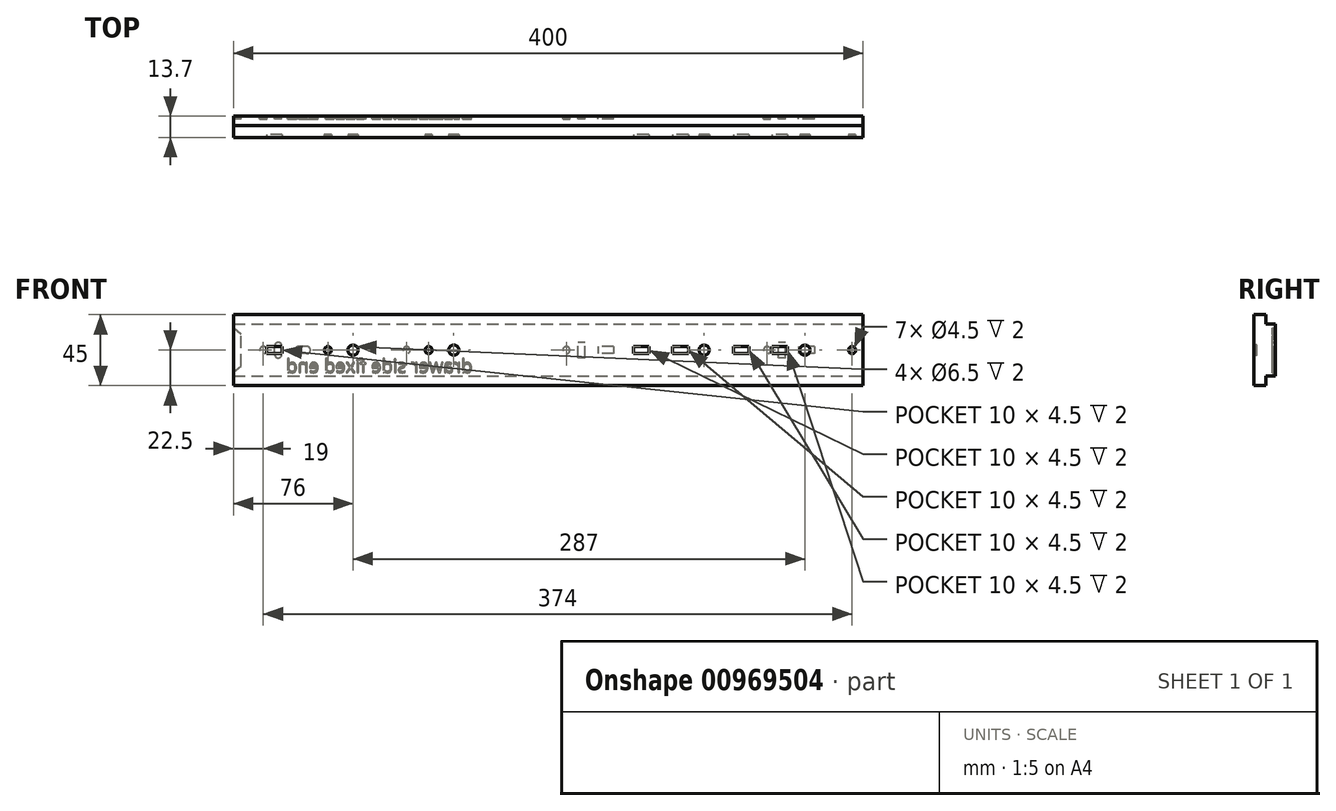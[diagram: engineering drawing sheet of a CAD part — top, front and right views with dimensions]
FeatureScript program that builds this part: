
annotation { "Feature Type Name" : "Feature", "Feature Type Description" : "" }
export const myFeature = defineFeature(function(context is Context, id is Id, definition is map)
    precondition{}
    {
        {
            var Q0;
            Q0=qCreatedBy(makeId("Front.planeOp"),FACE);
            var sketch = newSketch(context, id + "F0", { "sketchPlane" : qUnion([Q0])});
            skLineSegment(sketch, "E0.bottom", {"start": v(200, 22.5) * mm, "end": v(-200, 22.5) * mm});
            skLineSegment(sketch, "E0.top", {"start": v(200, -22.5) * mm, "end": v(-200, -22.5) * mm});
            skLineSegment(sketch, "E0.left", {"start": v(200, 22.5) * mm, "end": v(200, -22.5) * mm});
            skLineSegment(sketch, "E0.right", {"start": v(-200, 22.5) * mm, "end": v(-200, -22.5) * mm});
            skPoint(sketch, "E0.middle", {"position": v(0, 0) * mm});
            skSolve(sketch);
        }
        {
            var Q0;
            Q0=makeQuery(id+"F0.imprint","IMPRINT",FACE,{"disambiguationData":[TD([[makeQuery(id+"F0.imprint","IMPRINT",EDGE,{"derivedFrom":sQuery(id+"F0.wireOp",EDGE,"E0.bottom")}),1.0]])]});
            extrude(context, id + "F1", {"entities" : qUnion([Q0]), "depth" : 13.7 * mm, "offsetDistance" : 25 * mm});
        }
        {
            var Q0;
            Q0=makeQuery(id+"F1.opExtrude","CAP_FACE",FACE,{"disambiguationData":[OSD([sQuery(id+"F0.wireOp",EDGE,"E0.bottom"),sQuery(id+"F0.wireOp",EDGE,"E0.top"),sQuery(id+"F0.wireOp",EDGE,"E0.left"),sQuery(id+"F0.wireOp",EDGE,"E0.right")])],"isStart":false});
            var sketch = newSketch(context, id + "F2", { "sketchPlane" : qUnion([Q0])});
            skLineSegment(sketch, "E1", {"start": v(-200, 0) * mm, "end": v(200, 0) * mm, "construction": true});
            skCircle(sketch, "E2", {"center": v(-140, 0) * mm, "radius": 2.25 * mm});
            skCircle(sketch, "E3", {"center": v(-124, 0) * mm, "radius": 3.25 * mm});
            skCircle(sketch, "E4", {"center": v(-76, 0) * mm, "radius": 2.25 * mm});
            skCircle(sketch, "E5", {"center": v(-60, 0) * mm, "radius": 3.25 * mm});
            skLineSegment(sketch, "E6.bottom", {"start": v(-169, -2.25) * mm, "end": v(-179, -2.25) * mm});
            skLineSegment(sketch, "E6.top", {"start": v(-169, 2.25) * mm, "end": v(-179, 2.25) * mm});
            skLineSegment(sketch, "E6.left", {"start": v(-169, -2.25) * mm, "end": v(-169, 2.25) * mm});
            skLineSegment(sketch, "E6.right", {"start": v(-179, -2.25) * mm, "end": v(-179, 2.25) * mm});
            skPoint(sketch, "E6.middle", {"position": v(-174, 0) * mm});
            skLineSegment(sketch, "E7.bottom", {"start": v(64, 2.25) * mm, "end": v(54, 2.25) * mm});
            skLineSegment(sketch, "E7.top", {"start": v(64, -2.25) * mm, "end": v(54, -2.25) * mm});
            skLineSegment(sketch, "E7.left", {"start": v(64, 2.25) * mm, "end": v(64, -2.25) * mm});
            skLineSegment(sketch, "E7.right", {"start": v(54, 2.25) * mm, "end": v(54, -2.25) * mm});
            skPoint(sketch, "E7.middle", {"position": v(59, 0) * mm});
            skLineSegment(sketch, "E8.bottom", {"start": v(89, -2.25) * mm, "end": v(79, -2.25) * mm});
            skLineSegment(sketch, "E8.top", {"start": v(89, 2.25) * mm, "end": v(79, 2.25) * mm});
            skLineSegment(sketch, "E8.left", {"start": v(89, -2.25) * mm, "end": v(89, 2.25) * mm});
            skLineSegment(sketch, "E8.right", {"start": v(79, -2.25) * mm, "end": v(79, 2.25) * mm});
            skPoint(sketch, "E8.middle", {"position": v(84, 0) * mm});
            skCircle(sketch, "E9", {"center": v(99, 0) * mm, "radius": 3.25 * mm});
            skLineSegment(sketch, "E10.bottom", {"start": v(127.5, -2.25) * mm, "end": v(117.5, -2.25) * mm});
            skLineSegment(sketch, "E10.top", {"start": v(127.5, 2.25) * mm, "end": v(117.5, 2.25) * mm});
            skLineSegment(sketch, "E10.left", {"start": v(127.5, -2.25) * mm, "end": v(127.5, 2.25) * mm});
            skLineSegment(sketch, "E10.right", {"start": v(117.5, -2.25) * mm, "end": v(117.5, 2.25) * mm});
            skPoint(sketch, "E10.middle", {"position": v(122.5, 0) * mm});
            skLineSegment(sketch, "E11.bottom", {"start": v(152, -2.25) * mm, "end": v(142, -2.25) * mm});
            skLineSegment(sketch, "E11.top", {"start": v(152, 2.25) * mm, "end": v(142, 2.25) * mm});
            skLineSegment(sketch, "E11.left", {"start": v(152, -2.25) * mm, "end": v(152, 2.25) * mm});
            skLineSegment(sketch, "E11.right", {"start": v(142, -2.25) * mm, "end": v(142, 2.25) * mm});
            skPoint(sketch, "E11.middle", {"position": v(147, 0) * mm});
            skCircle(sketch, "E12", {"center": v(163, 0) * mm, "radius": 3.25 * mm});
            skCircle(sketch, "E13", {"center": v(193, 0) * mm, "radius": 2.25 * mm});
            skSolve(sketch);
        }
        {
            var Q0;
            Q0 = qSketchRegion(id + "F2", true);
            extrude(context, id + "F3", {"entities" : qUnion([Q0]), "operationType" : NewBodyOperationType.REMOVE, "oppositeDirection" : true, "depth" : 2 * mm, "offsetDistance" : 25 * mm});
        }
        {
            var Q0;
            Q0=makeQuery(id+"F1.opExtrude","CAP_FACE",FACE,{"disambiguationData":[OSD([sQuery(id+"F0.wireOp",EDGE,"E0.bottom"),sQuery(id+"F0.wireOp",EDGE,"E0.top"),sQuery(id+"F0.wireOp",EDGE,"E0.left"),sQuery(id+"F0.wireOp",EDGE,"E0.right")])],"isStart":true});
            var sketch = newSketch(context, id + "F4", { "sketchPlane" : qUnion([Q0])});
            skLineSegment(sketch, "E14", {"start": v(200, 0) * mm, "end": v(-200, 0) * mm, "construction": true});
            skLineSegment(sketch, "E15", {"start": v(195, -10) * mm, "end": v(195, 10) * mm});
            skLineSegment(sketch, "E16", {"start": v(195, 10) * mm, "end": v(200, 14) * mm});
            skLineSegment(sketch, "E17", {"start": v(200, 14) * mm, "end": v(200, -14) * mm});
            skLineSegment(sketch, "E18", {"start": v(200, -14) * mm, "end": v(195, -10) * mm});
            skCircle(sketch, "E19", {"center": v(181, 0) * mm, "radius": 2.25 * mm});
            skLineSegment(sketch, "E20.bottom", {"start": v(169.25, -5) * mm, "end": v(173.75, -5) * mm});
            skLineSegment(sketch, "E20.top", {"start": v(169.25, 5) * mm, "end": v(173.75, 5) * mm});
            skLineSegment(sketch, "E20.left", {"start": v(169.25, -5) * mm, "end": v(169.25, 5) * mm});
            skLineSegment(sketch, "E20.right", {"start": v(173.75, -5) * mm, "end": v(173.75, 5) * mm});
            skPoint(sketch, "E20.middle", {"position": v(171.5, 0) * mm});
            skLineSegment(sketch, "E21.bottom", {"start": v(151, 2.25) * mm, "end": v(161, 2.25) * mm});
            skLineSegment(sketch, "E21.top", {"start": v(151, -2.25) * mm, "end": v(161, -2.25) * mm});
            skLineSegment(sketch, "E21.left", {"start": v(151, 2.25) * mm, "end": v(151, -2.25) * mm});
            skLineSegment(sketch, "E21.right", {"start": v(161, 2.25) * mm, "end": v(161, -2.25) * mm});
            skPoint(sketch, "E21.middle", {"position": v(156, 0) * mm});
            skCircle(sketch, "E22", {"center": v(90, 0) * mm, "radius": 2.25 * mm});
            skCircle(sketch, "E23", {"center": v(-11.5, 0) * mm, "radius": 2.25 * mm});
            skLineSegment(sketch, "E24.bottom", {"start": v(-23.25, -5) * mm, "end": v(-18.75, -5) * mm});
            skLineSegment(sketch, "E24.top", {"start": v(-23.25, 5) * mm, "end": v(-18.75, 5) * mm});
            skLineSegment(sketch, "E24.left", {"start": v(-23.25, -5) * mm, "end": v(-23.25, 5) * mm});
            skLineSegment(sketch, "E24.right", {"start": v(-18.75, -5) * mm, "end": v(-18.75, 5) * mm});
            skPoint(sketch, "E24.middle", {"position": v(-21, 0) * mm});
            skLineSegment(sketch, "E25.bottom", {"start": v(-41.5, 2.25) * mm, "end": v(-31.5, 2.25) * mm});
            skLineSegment(sketch, "E25.top", {"start": v(-41.5, -2.25) * mm, "end": v(-31.5, -2.25) * mm});
            skLineSegment(sketch, "E25.left", {"start": v(-41.5, 2.25) * mm, "end": v(-41.5, -2.25) * mm});
            skLineSegment(sketch, "E25.right", {"start": v(-31.5, 2.25) * mm, "end": v(-31.5, -2.25) * mm});
            skPoint(sketch, "E25.middle", {"position": v(-36.5, 0) * mm});
            skCircle(sketch, "E26", {"center": v(-139, 0) * mm, "radius": 2.25 * mm});
            skLineSegment(sketch, "E27.bottom", {"start": v(-150.75, -5) * mm, "end": v(-146.25, -5) * mm});
            skLineSegment(sketch, "E27.top", {"start": v(-150.75, 5) * mm, "end": v(-146.25, 5) * mm});
            skLineSegment(sketch, "E27.left", {"start": v(-150.75, -5) * mm, "end": v(-150.75, 5) * mm});
            skLineSegment(sketch, "E27.right", {"start": v(-146.25, -5) * mm, "end": v(-146.25, 5) * mm});
            skPoint(sketch, "E27.middle", {"position": v(-148.5, 0) * mm});
            skLineSegment(sketch, "E28.bottom", {"start": v(-169, 2.25) * mm, "end": v(-159, 2.25) * mm});
            skLineSegment(sketch, "E28.top", {"start": v(-169, -2.25) * mm, "end": v(-159, -2.25) * mm});
            skLineSegment(sketch, "E28.left", {"start": v(-169, 2.25) * mm, "end": v(-169, -2.25) * mm});
            skLineSegment(sketch, "E28.right", {"start": v(-159, 2.25) * mm, "end": v(-159, -2.25) * mm});
            skPoint(sketch, "E28.middle", {"position": v(-164, 0) * mm});
            skSolve(sketch);
        }
        {
            var Q0;
            Q0 = qSketchRegion(id + "F4", true);
            extrude(context, id + "F5", {"entities" : qUnion([Q0]), "operationType" : NewBodyOperationType.REMOVE, "oppositeDirection" : true, "depth" : 2 * mm, "offsetDistance" : 25 * mm});
        }
        {
            var Q0;
            Q0=makeQuery(id+"F1.opExtrude","CAP_FACE",FACE,{"disambiguationData":[OSD([sQuery(id+"F0.wireOp",EDGE,"E0.bottom"),sQuery(id+"F0.wireOp",EDGE,"E0.top"),sQuery(id+"F0.wireOp",EDGE,"E0.left"),sQuery(id+"F0.wireOp",EDGE,"E0.right")])],"isStart":true});
            var sketch = newSketch(context, id + "F6", { "sketchPlane" : qUnion([Q0])});
            skLineSegment(sketch, "E29.bottom", {"start": v(200, -22.5) * mm, "end": v(-200, -22.5) * mm});
            skLineSegment(sketch, "E29.top", {"start": v(200, -16.5) * mm, "end": v(-200, -16.5) * mm});
            skLineSegment(sketch, "E29.left", {"start": v(200, -22.5) * mm, "end": v(200, -16.5) * mm});
            skLineSegment(sketch, "E29.right", {"start": v(-200, -22.5) * mm, "end": v(-200, -16.5) * mm});
            skLineSegment(sketch, "E30.bottom", {"start": v(200, 22.5) * mm, "end": v(-200, 22.5) * mm});
            skLineSegment(sketch, "E30.top", {"start": v(200, 16.5) * mm, "end": v(-200, 16.5) * mm});
            skLineSegment(sketch, "E30.left", {"start": v(200, 22.5) * mm, "end": v(200, 16.5) * mm});
            skLineSegment(sketch, "E30.right", {"start": v(-200, 22.5) * mm, "end": v(-200, 16.5) * mm});
            skSolve(sketch);
        }
        {
            var Q0;
            Q0=makeQuery(id+"F6.imprint","IMPRINT",FACE,{"disambiguationData":[TD([[makeQuery(id+"F6.imprint","IMPRINT",EDGE,{"derivedFrom":sQuery(id+"F6.wireOp",EDGE,"E29.bottom")}),1.0]])]});
            var Q1;
            Q1=makeQuery(id+"F6.imprint","IMPRINT",FACE,{"disambiguationData":[TD([[makeQuery(id+"F6.imprint","IMPRINT",EDGE,{"derivedFrom":sQuery(id+"F6.wireOp",EDGE,"E30.bottom")}),-1.0]])]});
            extrude(context, id + "F7", {"entities" : qUnion([Q0, Q1]), "operationType" : NewBodyOperationType.REMOVE, "oppositeDirection" : true, "depth" : 6 * mm, "offsetDistance" : 25 * mm});
        }
        {
            var Q0;
            Q0=makeQuery(id+"F5.boolean.opBoolean","COPY",EDGE,{"derivedFrom":makeQuery(id+"F5.opExtrude","SWEPT_EDGE",EDGE,{"disambiguationData":[OSD([sQuery(id+"F4.wireOp",EDGE,"E20.top"),sQuery(id+"F4.wireOp",EDGE,"E20.right")])]})});
            var Q1;
            Q1=makeQuery(id+"F5.boolean.opBoolean","COPY",EDGE,{"derivedFrom":makeQuery(id+"F5.opExtrude","SWEPT_EDGE",EDGE,{"disambiguationData":[OSD([sQuery(id+"F4.wireOp",EDGE,"E20.bottom"),sQuery(id+"F4.wireOp",EDGE,"E20.right")])]})});
            var Q2;
            Q2=makeQuery(id+"F5.boolean.opBoolean","COPY",EDGE,{"derivedFrom":makeQuery(id+"F5.opExtrude","SWEPT_EDGE",EDGE,{"disambiguationData":[OSD([sQuery(id+"F4.wireOp",EDGE,"E20.bottom"),sQuery(id+"F4.wireOp",EDGE,"E20.left")])]})});
            var Q3;
            Q3=makeQuery(id+"F5.boolean.opBoolean","COPY",EDGE,{"derivedFrom":makeQuery(id+"F5.opExtrude","SWEPT_EDGE",EDGE,{"disambiguationData":[OSD([sQuery(id+"F4.wireOp",EDGE,"E20.top"),sQuery(id+"F4.wireOp",EDGE,"E20.left")])]})});
            var Q4;
            Q4=makeQuery(id+"F5.boolean.opBoolean","COPY",EDGE,{"derivedFrom":makeQuery(id+"F5.opExtrude","SWEPT_EDGE",EDGE,{"disambiguationData":[OSD([sQuery(id+"F4.wireOp",EDGE,"E21.bottom"),sQuery(id+"F4.wireOp",EDGE,"E21.left")])]})});
            var Q5;
            Q5=makeQuery(id+"F5.boolean.opBoolean","COPY",EDGE,{"derivedFrom":makeQuery(id+"F5.opExtrude","SWEPT_EDGE",EDGE,{"disambiguationData":[OSD([sQuery(id+"F4.wireOp",EDGE,"E21.top"),sQuery(id+"F4.wireOp",EDGE,"E21.right")])]})});
            var Q6;
            Q6=makeQuery(id+"F5.boolean.opBoolean","COPY",EDGE,{"derivedFrom":makeQuery(id+"F5.opExtrude","SWEPT_EDGE",EDGE,{"disambiguationData":[OSD([sQuery(id+"F4.wireOp",EDGE,"E21.bottom"),sQuery(id+"F4.wireOp",EDGE,"E21.right")])]})});
            var Q7;
            Q7=makeQuery(id+"F5.boolean.opBoolean","COPY",EDGE,{"derivedFrom":makeQuery(id+"F5.opExtrude","SWEPT_EDGE",EDGE,{"disambiguationData":[OSD([sQuery(id+"F4.wireOp",EDGE,"E21.top"),sQuery(id+"F4.wireOp",EDGE,"E21.left")])]})});
            fillet(context, id + "F8", {"entities" : qUnion([Q0, Q1, Q2, Q3, Q4, Q5, Q6, Q7]), "radius" : 2.35 * mm, "tangentPropagation" : true, "allowEdgeOverflow" : false});
        }
        {
            var Q0;
            Q0=makeQuery(id+"F1.opExtrude","CAP_FACE",FACE,{"disambiguationData":[OSD([sQuery(id+"F0.wireOp",EDGE,"E0.bottom"),sQuery(id+"F0.wireOp",EDGE,"E0.top"),sQuery(id+"F0.wireOp",EDGE,"E0.left"),sQuery(id+"F0.wireOp",EDGE,"E0.right")])],"isStart":true});
            var sketch = newSketch(context, id + "F9", { "sketchPlane" : qUnion([Q0])});
            skText(sketch, "E31", { "text": "drawer side fixed end\n", "fontName": "OpenSans-Regular.ttf"});
            const initialGuessF9  = {"E31": [0.04815, -0.01424, 1, 0, 0.00845]};
            skSetInitialGuess(sketch, initialGuessF9);
            skSolve(sketch);
        }
        {
            var Q0;
            Q0 = qSketchRegion(id + "F9", true);
            extrude(context, id + "F10", {"entities" : qUnion([Q0]), "operationType" : NewBodyOperationType.REMOVE, "oppositeDirection" : true, "depth" : 2 * mm, "offsetDistance" : 25 * mm});
        }
    });
